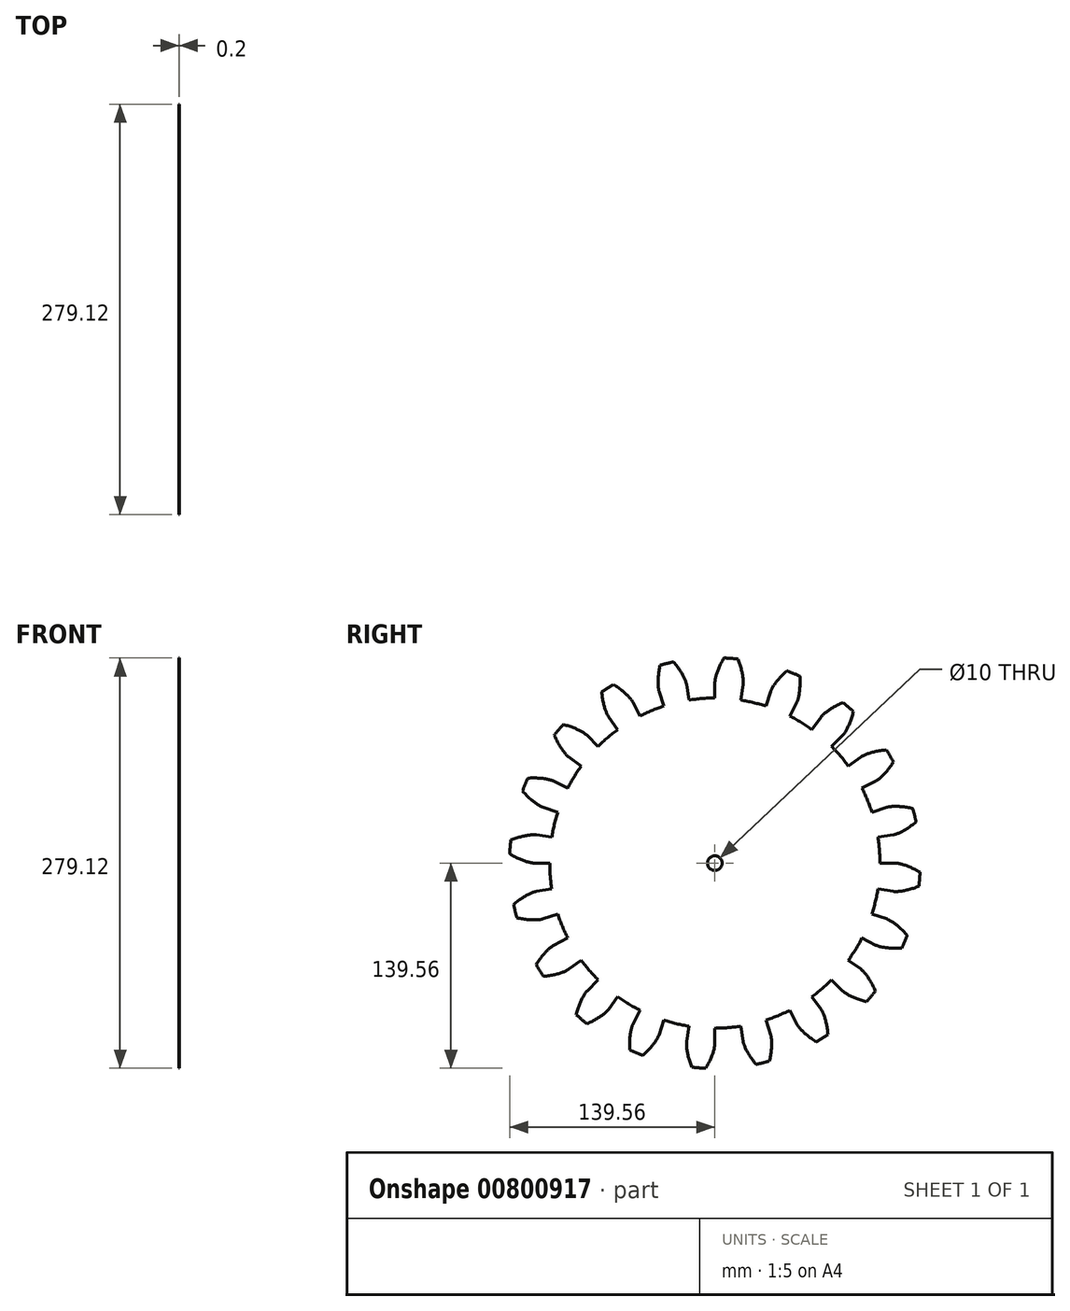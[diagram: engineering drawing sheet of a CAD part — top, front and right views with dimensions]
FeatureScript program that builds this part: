
annotation { "Feature Type Name" : "Feature", "Feature Type Description" : "" }
export const myFeature = defineFeature(function(context is Context, id is Id, definition is map)
    precondition{}
    {
        {
            assignVariable(context, id + "F0", {"name" : "NumberTeeth", "anyValue" : 20});
        }
        {
            assignVariable(context, id + "F1", {"name" : "GearThickness", "anyValue" : 0.2});
        }
        {
            var Q0;
            Q0=qCreatedBy(makeId("Right.planeOp"),FACE);
            var sketch = newSketch(context, id + "F2", { "sketchPlane" : qUnion([Q0])});
            skCircle(sketch, "E0", {"center": v(0, 0) * mm, "radius": 112.3 * mm});
            skCircle(sketch, "E1", {"center": v(0, 0) * mm, "radius": 122.95 * mm, "construction": true});
            skCircle(sketch, "E2", {"center": v(0, 0) * mm, "radius": 127 * mm, "construction": true});
            skCircle(sketch, "E3", {"center": v(0, 0) * mm, "radius": 139.7 * mm});
            skLineSegment(sketch, "E4", {"start": v(0, 0) * mm, "end": v(-122.95, 0) * mm, "construction": true});
            skLineSegment(sketch, "E5.1.0", {"start": v(0, 0) * mm, "end": v(-122.8, 6.15) * mm, "construction": true});
            skLineSegment(sketch, "E5.2.0", {"start": v(0, 0) * mm, "end": v(-122.34, 12.27) * mm, "construction": true});
            skLineSegment(sketch, "E5.3.0", {"start": v(0, 0) * mm, "end": v(-121.57, 18.37) * mm, "construction": true});
            skLineSegment(sketch, "E5.4.0", {"start": v(0, 0) * mm, "end": v(-120.5, 24.43) * mm, "construction": true});
            skLineSegment(sketch, "E5.5.0", {"start": v(0, 0) * mm, "end": v(-119.13, 30.42) * mm, "construction": true});
            skLineSegment(sketch, "E5.6.0", {"start": v(0, 0) * mm, "end": v(-117.46, 36.34) * mm, "construction": true});
            skLineSegment(sketch, "E5.7.0", {"start": v(0, 0) * mm, "end": v(-115.5, 42.16) * mm, "construction": true});
            skLineSegment(sketch, "E5.8.0", {"start": v(0, 0) * mm, "end": v(-113.25, 47.88) * mm, "construction": true});
            skLineSegment(sketch, "E5.9.0", {"start": v(0, 0) * mm, "end": v(-110.71, 53.48) * mm, "construction": true});
            skLineSegment(sketch, "E5.10.0", {"start": v(0, 0) * mm, "end": v(-107.9, 58.95) * mm, "construction": true});
            skLineSegment(sketch, "E5.11.0", {"start": v(0, 0) * mm, "end": v(-104.82, 64.27) * mm, "construction": true});
            skLineSegment(sketch, "E5.12.0", {"start": v(0, 0) * mm, "end": v(-101.48, 69.43) * mm, "construction": true});
            skLineSegment(sketch, "E5.13.0", {"start": v(0, 0) * mm, "end": v(-97.88, 74.41) * mm, "construction": true});
            skLineSegment(sketch, "E5.14.0", {"start": v(0, 0) * mm, "end": v(-94.04, 79.2) * mm, "construction": true});
            skLineSegment(sketch, "E5.anchor2", {"start": v(0, 0) * mm, "end": v(-94.04, 79.2) * mm, "construction": true});
            skLineSegment(sketch, "E6", {"start": v(-122.8, 6.15) * mm, "end": v(-123.1, 0) * mm, "construction": true});
            skLineSegment(sketch, "E7", {"start": v(-122.34, 12.27) * mm, "end": v(-123.57, 0.04) * mm, "construction": true});
            skLineSegment(sketch, "E8", {"start": v(-121.57, 18.37) * mm, "end": v(-124.33, 0.14) * mm, "construction": true});
            skLineSegment(sketch, "E9", {"start": v(-119.13, 30.42) * mm, "end": v(-126.74, 0.64) * mm, "construction": true});
            skLineSegment(sketch, "E10", {"start": v(-117.46, 36.34) * mm, "end": v(-128.36, 1.1) * mm, "construction": true});
            skLineSegment(sketch, "E11", {"start": v(-115.5, 42.16) * mm, "end": v(-130.26, 1.74) * mm, "construction": true});
            skLineSegment(sketch, "E12", {"start": v(-113.25, 47.88) * mm, "end": v(-132.4, 2.58) * mm, "construction": true});
            skLineSegment(sketch, "E13", {"start": v(-110.71, 53.48) * mm, "end": v(-134.78, 3.66) * mm, "construction": true});
            skLineSegment(sketch, "E14", {"start": v(-107.9, 58.95) * mm, "end": v(-137.38, 5) * mm, "construction": true});
            skLineSegment(sketch, "E15", {"start": v(-104.82, 64.27) * mm, "end": v(-140.17, 6.61) * mm, "construction": true});
            skLineSegment(sketch, "E16", {"start": v(-120.5, 24.43) * mm, "end": v(-125.39, 0.33) * mm, "construction": true});
            skLineSegment(sketch, "E17", {"start": v(-101.48, 69.43) * mm, "end": v(-143.13, 8.54) * mm, "construction": true});
            skLineSegment(sketch, "E18", {"start": v(-97.88, 74.41) * mm, "end": v(-146.25, 10.79) * mm, "construction": true});
            skLineSegment(sketch, "E19", {"start": v(-94.04, 79.2) * mm, "end": v(-149.49, 13.38) * mm, "construction": true});
            skLineSegment(sketch, "E20", {"start": v(0, 0) * mm, "end": v(-122.58, 9.65) * mm, "construction": true});
            skLineSegment(sketch, "E21", {"start": v(-112.3, 0) * mm, "end": v(-122.95, 0) * mm});
            skLineSegment(sketch, "E22.MirrorCS", {"start": v(-110.92, 17.57) * mm, "end": v(-121.44, 19.23) * mm});
            skFitSpline(sketch, "E23", {"points": [v(-122.95, 0) * mm, v(-123.1, 0) * mm, v(-123.57, 0.04) * mm, v(-124.33, 0.14) * mm, v(-125.39, 0.33) * mm, v(-126.74, 0.64) * mm, v(-128.36, 1.1) * mm, v(-130.26, 1.74) * mm, v(-132.4, 2.58) * mm, v(-134.78, 3.66) * mm, v(-137.38, 5) * mm, v(-140.17, 6.61) * mm, v(-143.13, 8.54) * mm, v(-146.25, 10.79) * mm, v(-149.49, 13.38) * mm], "startDerivative": vector(-0.1, 0) * mm, "endDerivative": vector(-4.07, 3.43) * mm});
            skLineSegment(sketch, "E24", {"start": v(-67.55, -55.63) * mm, "end": v(-149.49, 13.38) * mm, "construction": true});
            skFitSpline(sketch, "E25.MirrorCS", {"points": [v(-121.44, 19.23) * mm, v(-121.6, 19.25) * mm, v(-122.05, 19.29) * mm, v(-122.82, 19.31) * mm, v(-123.9, 19.3) * mm, v(-125.28, 19.2) * mm, v(-126.96, 19) * mm, v(-128.92, 18.66) * mm, v(-131.17, 18.16) * mm, v(-133.7, 17.47) * mm, v(-136.47, 16.56) * mm, v(-139.48, 15.4) * mm, v(-142.7, 13.96) * mm, v(-146.14, 12.22) * mm, v(-149.74, 10.17) * mm], "startDerivative": vector(-0.09, 0.01) * mm, "endDerivative": vector(-4.56, -2.75) * mm});
            skSolve(sketch);
        }
        {
            var Q0;
            {var subQ0=sQuery(id+"F2.wireOp",EDGE,"E0");var subQ27=makeQuery(id+"F2.imprint","INTERSECT",VERTEX,{"derivedFrom":[subQ0,sQuery(id+"F2.wireOp",EDGE,"10ea1024-8cf5-41f5-a75f-a634b86921f3.10.0")]});Q0=makeQuery(id+"F2.imprint","IMPRINT",FACE,{"disambiguationData":[TD([[makeQuery(id+"F2.imprint","IMPRINT",EDGE,{"disambiguationData":[TD([[subQ27,-1.0]])],"derivedFrom":subQ0}),1.0]])]});}
            var Q1;
            {var subQ0=sQuery(id+"F2.wireOp",EDGE,"10ea1024-8cf5-41f5-a75f-a634b86921f3.1.0");Q1=makeQuery(id+"F2.imprint","IMPRINT",FACE,{"disambiguationData":[TD([[makeQuery(id+"F2.imprint","IMPRINT",EDGE,{"derivedFrom":subQ0}),-1.0]])]});}
            var Q2;
            {var subQ7=sQuery(id+"F2.wireOp",EDGE,"10ea1024-8cf5-41f5-a75f-a634b86921f3.2.0");Q2=makeQuery(id+"F2.imprint","IMPRINT",FACE,{"disambiguationData":[TD([[makeQuery(id+"F2.imprint","IMPRINT",EDGE,{"derivedFrom":subQ7}),-1.0]])]});}
            var Q3;
            {var subQ8=sQuery(id+"F2.wireOp",EDGE,"10ea1024-8cf5-41f5-a75f-a634b86921f3.3.0");Q3=makeQuery(id+"F2.imprint","IMPRINT",FACE,{"disambiguationData":[TD([[makeQuery(id+"F2.imprint","IMPRINT",EDGE,{"derivedFrom":subQ8}),-1.0]])]});}
            var Q4;
            {var subQ2=sQuery(id+"F2.wireOp",EDGE,"10ea1024-8cf5-41f5-a75f-a634b86921f3.4.0");Q4=makeQuery(id+"F2.imprint","IMPRINT",FACE,{"disambiguationData":[TD([[makeQuery(id+"F2.imprint","IMPRINT",EDGE,{"derivedFrom":subQ2}),-1.0]])]});}
            var Q5;
            {var subQ8=sQuery(id+"F2.wireOp",EDGE,"10ea1024-8cf5-41f5-a75f-a634b86921f3.5.0");Q5=makeQuery(id+"F2.imprint","IMPRINT",FACE,{"disambiguationData":[TD([[makeQuery(id+"F2.imprint","IMPRINT",EDGE,{"derivedFrom":subQ8}),-1.0]])]});}
            var Q6;
            {var subQ3=sQuery(id+"F2.wireOp",EDGE,"10ea1024-8cf5-41f5-a75f-a634b86921f3.6.0");Q6=makeQuery(id+"F2.imprint","IMPRINT",FACE,{"disambiguationData":[TD([[makeQuery(id+"F2.imprint","IMPRINT",EDGE,{"derivedFrom":subQ3}),-1.0]])]});}
            var Q7;
            {var subQ0=sQuery(id+"F2.wireOp",EDGE,"10ea1024-8cf5-41f5-a75f-a634b86921f3.7.0");Q7=makeQuery(id+"F2.imprint","IMPRINT",FACE,{"disambiguationData":[TD([[makeQuery(id+"F2.imprint","IMPRINT",EDGE,{"derivedFrom":subQ0}),-1.0]])]});}
            var Q8;
            {var subQ5=sQuery(id+"F2.wireOp",EDGE,"10ea1024-8cf5-41f5-a75f-a634b86921f3.8.0");Q8=makeQuery(id+"F2.imprint","IMPRINT",FACE,{"disambiguationData":[TD([[makeQuery(id+"F2.imprint","IMPRINT",EDGE,{"derivedFrom":subQ5}),-1.0]])]});}
            var Q9;
            {var subQ1=sQuery(id+"F2.wireOp",EDGE,"10ea1024-8cf5-41f5-a75f-a634b86921f3.9.0");Q9=makeQuery(id+"F2.imprint","IMPRINT",FACE,{"disambiguationData":[TD([[makeQuery(id+"F2.imprint","IMPRINT",EDGE,{"derivedFrom":subQ1}),-1.0]])]});}
            var Q10;
            {var subQ5=sQuery(id+"F2.wireOp",EDGE,"10ea1024-8cf5-41f5-a75f-a634b86921f3.10.0");Q10=makeQuery(id+"F2.imprint","IMPRINT",FACE,{"disambiguationData":[TD([[makeQuery(id+"F2.imprint","IMPRINT",EDGE,{"derivedFrom":subQ5}),-1.0]])]});}
            var Q11;
            {var subQ8=sQuery(id+"F2.wireOp",EDGE,"10ea1024-8cf5-41f5-a75f-a634b86921f3.11.0");Q11=makeQuery(id+"F2.imprint","IMPRINT",FACE,{"disambiguationData":[TD([[makeQuery(id+"F2.imprint","IMPRINT",EDGE,{"derivedFrom":subQ8}),-1.0]])]});}
            var Q12;
            {var subQ2=sQuery(id+"F2.wireOp",EDGE,"10ea1024-8cf5-41f5-a75f-a634b86921f3.12.0");Q12=makeQuery(id+"F2.imprint","IMPRINT",FACE,{"disambiguationData":[TD([[makeQuery(id+"F2.imprint","IMPRINT",EDGE,{"derivedFrom":subQ2}),-1.0]])]});}
            var Q13;
            {var subQ3=sQuery(id+"F2.wireOp",EDGE,"10ea1024-8cf5-41f5-a75f-a634b86921f3.13.0");Q13=makeQuery(id+"F2.imprint","IMPRINT",FACE,{"disambiguationData":[TD([[makeQuery(id+"F2.imprint","IMPRINT",EDGE,{"derivedFrom":subQ3}),-1.0]])]});}
            var Q14;
            {var subQ0=sQuery(id+"F2.wireOp",EDGE,"10ea1024-8cf5-41f5-a75f-a634b86921f3.14.0");Q14=makeQuery(id+"F2.imprint","IMPRINT",FACE,{"disambiguationData":[TD([[makeQuery(id+"F2.imprint","IMPRINT",EDGE,{"derivedFrom":subQ0}),-1.0]])]});}
            var Q15;
            {var subQ6=sQuery(id+"F2.wireOp",EDGE,"10ea1024-8cf5-41f5-a75f-a634b86921f3.15.0");Q15=makeQuery(id+"F2.imprint","IMPRINT",FACE,{"disambiguationData":[TD([[makeQuery(id+"F2.imprint","IMPRINT",EDGE,{"derivedFrom":subQ6}),-1.0]])]});}
            var Q16;
            {var subQ5=sQuery(id+"F2.wireOp",EDGE,"10ea1024-8cf5-41f5-a75f-a634b86921f3.16.0");Q16=makeQuery(id+"F2.imprint","IMPRINT",FACE,{"disambiguationData":[TD([[makeQuery(id+"F2.imprint","IMPRINT",EDGE,{"derivedFrom":subQ5}),-1.0]])]});}
            var Q17;
            {var subQ7=sQuery(id+"F2.wireOp",EDGE,"10ea1024-8cf5-41f5-a75f-a634b86921f3.17.0");Q17=makeQuery(id+"F2.imprint","IMPRINT",FACE,{"disambiguationData":[TD([[makeQuery(id+"F2.imprint","IMPRINT",EDGE,{"derivedFrom":subQ7}),-1.0]])]});}
            var Q18;
            {var subQ5=sQuery(id+"F2.wireOp",EDGE,"10ea1024-8cf5-41f5-a75f-a634b86921f3.18.0");Q18=makeQuery(id+"F2.imprint","IMPRINT",FACE,{"disambiguationData":[TD([[makeQuery(id+"F2.imprint","IMPRINT",EDGE,{"derivedFrom":subQ5}),-1.0]])]});}
            var Q19;
            {var subQ8=sQuery(id+"F2.wireOp",EDGE,"10ea1024-8cf5-41f5-a75f-a634b86921f3.19.0");Q19=makeQuery(id+"F2.imprint","IMPRINT",FACE,{"disambiguationData":[TD([[makeQuery(id+"F2.imprint","IMPRINT",EDGE,{"derivedFrom":subQ8}),-1.0]])]});}
            var Q20;
            {var subQ8=sQuery(id+"F2.wireOp",EDGE,"E21");Q20=makeQuery(id+"F2.imprint","IMPRINT",FACE,{"disambiguationData":[TD([[makeQuery(id+"F2.imprint","IMPRINT",EDGE,{"derivedFrom":subQ8}),-1.0]])]});}
            extrude(context, id + "F3", {"entities" : qUnion([Q0, Q1, Q2, Q3, Q4, Q5, Q6, Q7, Q8, Q9, Q10, Q11, Q12, Q13, Q14, Q15, Q16, Q17, Q18, Q19, Q20]), "depth" : (getVariable(context, 'GearThickness')) * mm});
        }
        {
            var Q0;
            Q0=makeQuery(id+"F3.opExtrude","SWEPT_FACE",FACE,{"disambiguationData":[OSD([sQuery(id+"F2.wireOp",EDGE,"E25.MirrorCS")])]});
            var Q1;
            Q1=makeQuery(id+"F3.opExtrude","SWEPT_FACE",FACE,{"disambiguationData":[OSD([sQuery(id+"F2.wireOp",EDGE,"E23")])]});
            var Q2;
            Q2=makeQuery(id+"F3.opExtrude","SWEPT_FACE",FACE,{"disambiguationData":[OSD([sQuery(id+"F2.wireOp",EDGE,"E3")])]});
            var Q3;
            Q3=makeQuery(id+"F3.opExtrude","SWEPT_FACE",FACE,{"disambiguationData":[OSD([sQuery(id+"F2.wireOp",EDGE,"E22.MirrorCS")])]});
            var Q4;
            Q4=makeQuery(id+"F3.opExtrude","SWEPT_FACE",FACE,{"disambiguationData":[OSD([sQuery(id+"F2.wireOp",EDGE,"E21")])]});
            var Q5;
            Q5=makeQuery(id+"F3.opExtrude","SWEPT_FACE",FACE,{"disambiguationData":[OSD([sQuery(id+"F2.wireOp",EDGE,"E0")])]});
            circularPattern(context, id + "F4", {"faces" : qUnion([Q0, Q1, Q2, Q3, Q4]), "axis" : qUnion([Q5]), "angle" : 360 * degree, "instanceCount" : getVariable(context, 'NumberTeeth'), "equalSpace" : true, "patternType" : PatternType.FACE});
        }
        {
            var Q0;
            Q0=makeQuery(id+"F3.opExtrude","CAP_FACE",FACE,{"disambiguationData":[OSD([sQuery(id+"F2.wireOp",EDGE,"E0"),sQuery(id+"F2.wireOp",EDGE,"E3"),sQuery(id+"F2.wireOp",EDGE,"E21"),sQuery(id+"F2.wireOp",EDGE,"E22.MirrorCS"),sQuery(id+"F2.wireOp",EDGE,"E23"),sQuery(id+"F2.wireOp",EDGE,"E25.MirrorCS")])],"isStart":true});
            var sketch = newSketch(context, id + "F5", { "sketchPlane" : qUnion([Q0])});
            skCircle(sketch, "E26", {"center": v(0, 0) * mm, "radius": 5 * mm});
            skSolve(sketch);
        }
        {
            var Q0;
            Q0 = qSketchRegion(id + "F5", true);
            extrude(context, id + "F6", {"entities" : qUnion([Q0]), "operationType" : NewBodyOperationType.REMOVE, "endBound" : BoundingType.THROUGH_ALL, "oppositeDirection" : true, "depth" : 25 * mm, "offsetDistance" : 25 * mm});
        }
    });
